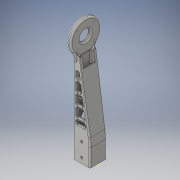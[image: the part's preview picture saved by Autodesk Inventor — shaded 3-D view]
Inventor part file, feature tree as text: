
AUTODESK INVENTOR PART (.ipt)
format: ipt  version: 2016 (Build 200138000, 138)  size: 1,760,256 bytes
history: native  units: in
note: dims shown in document units (in); Inventor stores cm internally (conversion verified against a paired STEP export)
features: fillet x23, sketch x18, extrude x14, plane x2, revolve x2, chamfer x2, loft x1, shell x1, mirror x1, other x1
ambient origin geometry x8: Origin, YZ Plane, XZ Plane, XY Plane, X Axis, Y Axis, Z Axis, Center Point
bodies: Solid1 (feature_tree)
feature tree (65):
  extrude  "Extrusion1"  Depth=1.5in
  plane  "Work Plane1"
  loft  "Loft1"
  revolve  "Revolution1"  Angle=90.0deg
  shell  "Shell1"  Thickness=0.0in
  extrude  "Extrusion2"  Depth=0.25in
  extrude  "Extrusion5"  Depth=1.25in
  extrude  "Extrusion3"  Depth=7.5in TaperAngle=0.0deg
  chamfer  "Chamfer1"  Distance=0.375in
  fillet  "Fillet1"  Radius=0.125in
  fillet  "Fillet2"  Radius=0.25in
  fillet  "Fillet3"  Radius=5.0in
  fillet  "Fillet4"  Radius=0.125in
  fillet  "Fillet5"  Radius=0.0312in
  extrude  "Extrusion6"  Depth=0.125in
  extrude  "Extrusion7"  Depth=0.125in
  extrude  "Extrusion8"  Depth=0.375in
  chamfer  "Chamfer2"  Distance=2.0in
  extrude  "Extrusion9"  Depth=0.125in TaperAngle=45.0deg
  extrude  "Extrusion10"  Depth=0.125in
  fillet  "Fillet6"  Radius=0.126in
  fillet  "Fillet8"  Radius=2.0in
  fillet  "Fillet9"  Radius=1.0in
  fillet  "Fillet10"  Radius=2.0in
  fillet  "Fillet11"  Radius=0.125in
  revolve  "Revolution2"  [1 undecoded]
  extrude  "Extrusion11"  Depth=0.0312in
  fillet  "Fillet12"  Radius=0.25in
  fillet  "Fillet13"  Radius=0.25in
  fillet  "Fillet14"  Radius=1.25in
  fillet  "Fillet15"  Radius=0.25in
  fillet  "Fillet16"  Radius=0.0515in
  sketch  "Sketch15"  dims[d56=0.125in d57=0.0312in]
  fillet  "Fillet17"  Radius=0.4375in
  extrude  "Extrusion12"  Depth=0.0625in
  extrude  "Extrusion13"  Depth=0.125in
  fillet  "Fillet20"  Radius=0.0312in
  fillet  "Fillet21"  Radius=0.0312in
  extrude  "Extrusion14"  Depth=0.0312in
  fillet  "Fillet27"  Radius=1.25in
  extrude  "Extrusion16"  Depth=0.0312in
  fillet  "Fillet28"  Radius=2.0in
  plane  "Work Plane2"
  mirror  "Mirror1"
  fillet  "Fillet29"  Radius=3.0in
  fillet  "Fillet30"  Radius=0.5in
  fillet  "Fillet31"  Radius=0.5in
  sketch  "Sketch1"  dims[d0=1.5in d1=1.5in]
  sketch  "Sketch2"  dims[d2=2.0in d3=0.0in d4=7.5in]
  other  "Edges1"
  sketch  "Sketch3"  dims[d5=0.375in d6=0.0in d7=90.0deg d8=0.0in d9=90.0deg]
  sketch  "Sketch4"  dims[d10=90.0deg d11=0.25in]
  sketch  "Sketch5"  dims[d12=1.25in d13=1.25in]
  sketch  "Sketch7"  dims[d14=2.5in d15=0.0in d17=7.5in d18=0.0in]
  sketch  "Sketch8"  dims[d21=2.75in d22=0.375in d23=0.0in d24=0.125in d25=0.25in]
  sketch  "Sketch9"  dims[d26=0.5in d27=0.125in d28=45.0deg d29=5.0in d30=0.125in d31=0.0312in]
  sketch  "Sketch10"  dims[d32=0.0312in d33=0.125in]
  sketch  "Sketch11"  dims[d34=1.5in d35=0.125in]
  sketch  "Sketch12"  dims[d36=0.375in d37=0.0in d38=0.625in d39=2.0in d40=0.0in]
  sketch  "Sketch13"  dims[d41=2.0in d42=0.0in d43=0.125in d44=0.125in d45=45.0deg]
  sketch  "Sketch14"  dims[d46=45.0deg d47=2.1732in d48=0.126in d49=2.0in d50=0.0in d51=1.0in d52=2.0in d53=0.0in d54=0.125in]
  sketch  "Sketch16"  dims[d58=0.0312in d59=0.0312in d60=0.25in d61=0.25in d62=1.25in d63=0.25in]
  sketch  "Sketch17"  dims[d64=1.5748in d66=1.0in d67=0.3937in d69=1.0in d71=0.0515in d74=0.4375in d75=0.0in]
  sketch  "Sketch18"  dims[d76=0.1in d77=0.0625in]
  sketch  "Sketch20"  dims[d78=0.05in d79=0.125in d80=0.0312in d81=0.0312in d82=0.5in d83=1.25in d84=0.2188in d85=2.0in d86=0.0in d87=3.0in d88=0.5in d89=0.5in d90=0.0in d93=0.5in d94=0.0625in d95=0.125in d96=0.25in d97=1.25in d98=0.325in d99=4.0in d100=0.25in d101=0.0in d116=0.0625in d117=0.0312in d118=0.0312in d119=0.0312in d120=0.0312in d121=0.5in d122=0.0in d123=0.0312in d124=0.625in d125=0.0312in d126=0.0312in d127=0.0312in]
note: 1 required parameter value undecoded (feature->parameter linkage not recoverable at this tier; creation-order binding heuristic only, values carry confidence <= 0.55)
